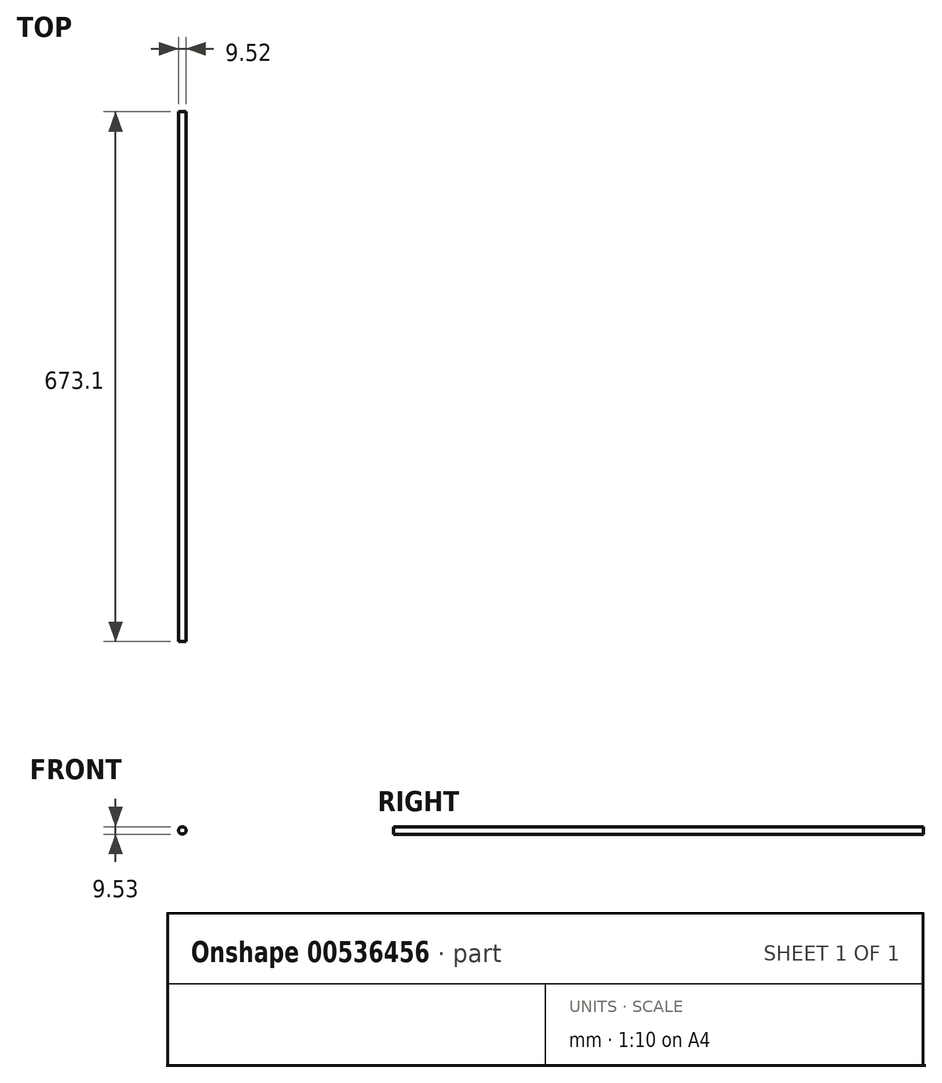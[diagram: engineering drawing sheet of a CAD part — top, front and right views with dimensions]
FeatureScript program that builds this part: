
annotation { "Feature Type Name" : "Feature", "Feature Type Description" : "" }
export const myFeature = defineFeature(function(context is Context, id is Id, definition is map)
    precondition{}
    {
        {
            var Q0;
            Q0=qCreatedBy(makeId("Front.planeOp"),FACE);
            var sketch = newSketch(context, id + "F0", { "sketchPlane" : qUnion([Q0])});
            skCircle(sketch, "E0", {"center": v(-9.8, 13.16) * mm, "radius": 4.76 * mm});
            skSolve(sketch);
        }
        {
            var Q0;
            Q0 = qSketchRegion(id + "F0", true);
            extrude(context, id + "F1", {"entities" : qUnion([Q0]), "depth" : 673.1 * mm, "offsetDistance" : 25.4 * mm});
        }
    });
